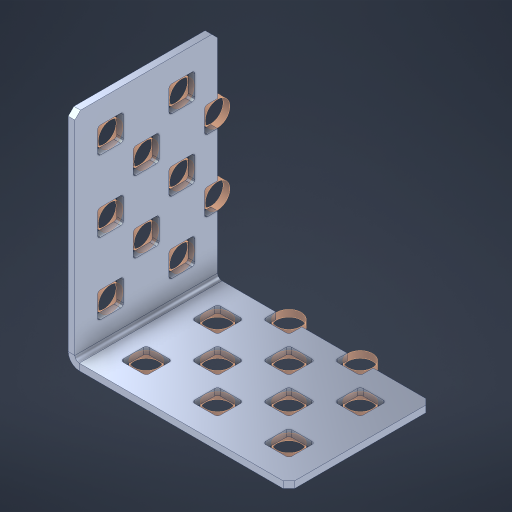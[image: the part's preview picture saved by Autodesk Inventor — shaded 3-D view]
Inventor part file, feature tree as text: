
AUTODESK INVENTOR PART (.ipt)
format: ipt  version: 2023 (Build 270158000, 158)  size: 550,912 bytes
history: native  units: in
note: dims shown in document units (in); Inventor stores cm internally (conversion verified against a paired STEP export)
features: other x26, extrude x18, sheet_metal_op x8, sketch x7, pattern_linear x3, mirror x1, chamfer x1
ambient origin geometry x8: Origin, YZ Plane, XZ Plane, XY Plane, X Axis, Y Axis, Z Axis, Center Point
bodies: Solid1 (feature_tree), Body (feature_tree)
feature tree (64):
  sheet_metal_op  "Flanges"
  sheet_metal_op  "Body Pattern"
  pattern_linear  "Center Double"  Spacing1=1.5in  [1 undecoded]
  pattern_linear  "Center Pattern"  Spacing1=0.1875in  [1 undecoded]
  other  "Arc Length"
  pattern_linear  "Notch Pattern"  Spacing1=0.0469in  [1 undecoded]
  other  "Diagonal Plane"
  mirror  "Everything Mirrored"
  chamfer  "End Chamfer"
  sketch  "Sketch1"  dims[d0=1.5in]
  other  "Plate1"
  sketch  "Sketch2"  dims[d1=1.0in]
  other  "Plate2"
  sheet_metal_op  "Bend1"
  sheet_metal_op  "Corner1"
  sketch  "Sketch8"  dims[d2=0.0469in]
  sketch  "Sketch9"  dims[d3=0.0469in]
  other  "Srf91"
  sheet_metal_op  "Body Pattern Sketch"
  other  "Srf92"
  sketch  "Sketch13"  dims[d4=0.0234in]
  sketch  "Sketch15"  dims[d5=0.0938in]
  sketch  "Sketch16"  dims[d6=0.0469in d7=1.5in d8=90.0deg d9=0.0312in d10=0.1875in d11=0.0469in d12=0.0469in d49=0.182in d50=0.02in d52=0.25in d53=0.0469in d54=0.0in d55=0.172in d56=1.0in d57=0.0in d85=0.1473in d86=0.1659in d89=0.0469in d90=0.0in d91=0.04in d92=0.0491in d95=2.5in d96=0.04in d97=0.25in d98=45.0deg d106=0.182in d107=0.02in d110=0.0469in d111=0.0in d112=0.172in d113=0.5in d114=0.0in d117=0.5in d126=0.0491in d127=0.1227in d128=0.08in d129=0.04in d130=2.5in d131=0.25in d132=0.7874in d134=0.5in d135=1.1811in d137=0.5in d140=0.5in d141=1.0in d142=0.3937in d144=0.5in d145=0.071in d146=0.7874in d148=0.5in]
  other  "Srf786"
  other  "Srf856"
  other  "Srf889"
  other  "Srf1275"
  other  "Srf1276"
  other  "Srf1278"
  other  "Srf1277"
  other  "Srf1285"
  other  "Srf2009"
  other  "Srf2010"
  other  "Srf2043"
  other  "Srf2076"
  other  "Srf2077"
  other  "Srf2078"
  other  "Srf2079"
  other  "Srf2179"
  other  "Srf2180"
  other  "Srf2181"
  sheet_metal_op  "Body Stamp"
  sheet_metal_op  "Body Circle"
  other  "Center Stamp"
  other  "Center Circle"
  sheet_metal_op  "Notch"
  extrude  "ExtrusionSrf92"  Depth=0.0469in
  extrude  "ExtrusionSrf856"  Depth=0.182in
  extrude  "ExtrusionSrf889"  Depth=0.02in
  extrude  "ExtrusionSrf1275"  Depth=0.25in
  extrude  "ExtrusionSrf1276"  Depth=0.0469in
  extrude  "ExtrusionSrf1277"  TaperAngle=0.0deg  [1 undecoded]
  extrude  "ExtrusionSrf1345"  Depth=0.5in
  extrude  "ExtrusionSrf1346"  Depth=1.0in TaperAngle=0.0deg
  extrude  "ExtrusionSrf2009"  Depth=0.5in
  extrude  "ExtrusionSrf2010"  Depth=0.5in
  extrude  "ExtrusionSrf2043"  Depth=0.0469in
  extrude  "ExtrusionSrf2076"  Depth=0.5in TaperAngle=0.0deg
  extrude  "ExtrusionSrf2077"  Depth=0.5in
  extrude  "ExtrusionSrf2078"  Depth=0.25in TaperAngle=45.0deg
  extrude  "ExtrusionSrf2079"  Depth=0.182in
  extrude  "ExtrusionSrf2179"  Depth=0.02in
  extrude  "ExtrusionSrf2180"  Depth=0.0469in
  extrude  "ExtrusionSrf2181"  TaperAngle=0.0deg  [1 undecoded]
note: 5 required parameter values undecoded (feature->parameter linkage not recoverable at this tier; creation-order binding heuristic only, values carry confidence <= 0.55)
